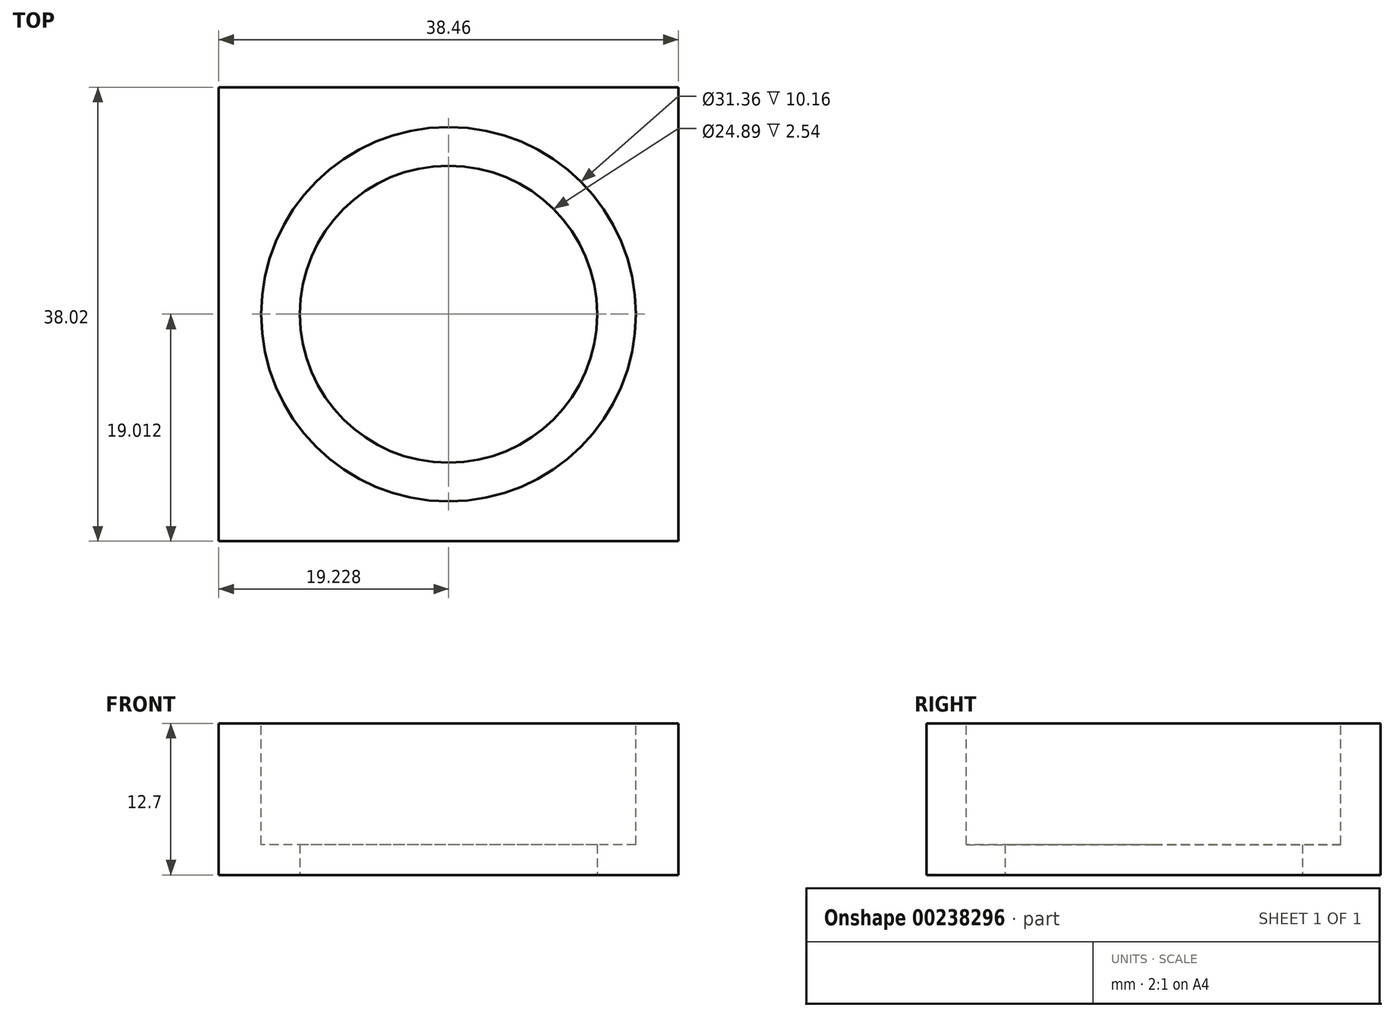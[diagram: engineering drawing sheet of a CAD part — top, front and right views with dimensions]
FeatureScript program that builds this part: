
annotation { "Feature Type Name" : "Feature", "Feature Type Description" : "" }
export const myFeature = defineFeature(function(context is Context, id is Id, definition is map)
    precondition{}
    {
        {
            var Q0;
            Q0=qCreatedBy(makeId("Top.planeOp"),FACE);
            var sketch = newSketch(context, id + "F0", { "sketchPlane" : qUnion([Q0])});
            skLineSegment(sketch, "E0.bottom", {"start": v(0, 0) * mm, "end": v(38.46, 0) * mm});
            skLineSegment(sketch, "E0.top", {"start": v(0, 38.02) * mm, "end": v(38.46, 38.02) * mm});
            skLineSegment(sketch, "E0.left", {"start": v(0, 0) * mm, "end": v(0, 38.02) * mm});
            skLineSegment(sketch, "E0.right", {"start": v(38.46, 0) * mm, "end": v(38.46, 38.02) * mm});
            skSolve(sketch);
        }
        {
            var Q0;
            Q0 = qSketchRegion(id + "F0", true);
            extrude(context, id + "F1", {"entities" : qUnion([Q0]), "depth" : 12.7 * mm});
        }
        {
            var Q0;
            Q0=makeQuery(id+"F1.opExtrude","CAP_FACE",FACE,{"disambiguationData":[OSD([sQuery(id+"F0.wireOp",EDGE,"E0.bottom"),sQuery(id+"F0.wireOp",EDGE,"E0.top"),sQuery(id+"F0.wireOp",EDGE,"E0.left"),sQuery(id+"F0.wireOp",EDGE,"E0.right")])],"isStart":false});
            var sketch = newSketch(context, id + "F2", { "sketchPlane" : qUnion([Q0])});
            skPoint(sketch, "E1.centerSnap0", {"position": v(19.23, 38.02) * mm});
            skCircle(sketch, "E2", {"center": v(19.23, 19.01) * mm, "radius": 15.68 * mm});
            skPoint(sketch, "E2.centerSnap0", {"position": v(38.46, 19.01) * mm});
            skSolve(sketch);
        }
        {
            var Q0;
            Q0=sQuery(id+"F2.wireOp",EDGE,"E2");
            extrude(context, id + "F3", {"bodyType" : ToolBodyType.SURFACE, "surfaceEntities" : qUnion([Q0]), "oppositeDirection" : true, "depth" : 10.16 * mm});
        }
        {
            var Q0;
            Q0=sQuery(id+"F2.wireOp",EDGE,"E2");
            extrude(context, id + "F4", {"bodyType" : ToolBodyType.SURFACE, "surfaceEntities" : qUnion([Q0]), "oppositeDirection" : true, "depth" : 12.7 * mm});
        }
        {
            var Q0;
            Q0=makeQuery(id+"F2.imprint","IMPRINT",FACE,{"disambiguationData":[TD([[makeQuery(id+"F2.imprint","IMPRINT",EDGE,{"derivedFrom":sQuery(id+"F2.wireOp",EDGE,"E2")}),1.0]])]});
            var Q1;
            Q1=sQuery(id+"F2.wireOp",EDGE,"E2");
            extrude(context, id + "F5", {"entities" : qUnion([Q0]), "operationType" : NewBodyOperationType.REMOVE, "surfaceEntities" : qUnion([Q1]), "oppositeDirection" : true, "depth" : 10.16 * mm});
        }
        {
            var Q0;
            Q0=makeQuery(id+"F1.opExtrude","CAP_FACE",FACE,{"disambiguationData":[OSD([sQuery(id+"F0.wireOp",EDGE,"E0.bottom"),sQuery(id+"F0.wireOp",EDGE,"E0.top"),sQuery(id+"F0.wireOp",EDGE,"E0.left"),sQuery(id+"F0.wireOp",EDGE,"E0.right")])],"isStart":true});
            var sketch = newSketch(context, id + "F6", { "sketchPlane" : qUnion([Q0])});
            skCircle(sketch, "E3", {"center": v(19.23, -19.01) * mm, "radius": 12.44 * mm});
            skPoint(sketch, "E3.centerSnap0", {"position": v(38.46, -19.01) * mm});
            skPoint(sketch, "E3.centerSnap1", {"position": v(19.23, 0) * mm});
            skSolve(sketch);
        }
        {
            var Q0;
            Q0=makeQuery(id+"F6.imprint","IMPRINT",FACE,{"disambiguationData":[TD([[makeQuery(id+"F6.imprint","IMPRINT",EDGE,{"derivedFrom":sQuery(id+"F6.wireOp",EDGE,"E3")}),1.0]])]});
            extrude(context, id + "F7", {"entities" : qUnion([Q0]), "operationType" : NewBodyOperationType.REMOVE, "endBound" : BoundingType.THROUGH_ALL, "oppositeDirection" : true, "depth" : 25.4 * mm});
        }
    });
